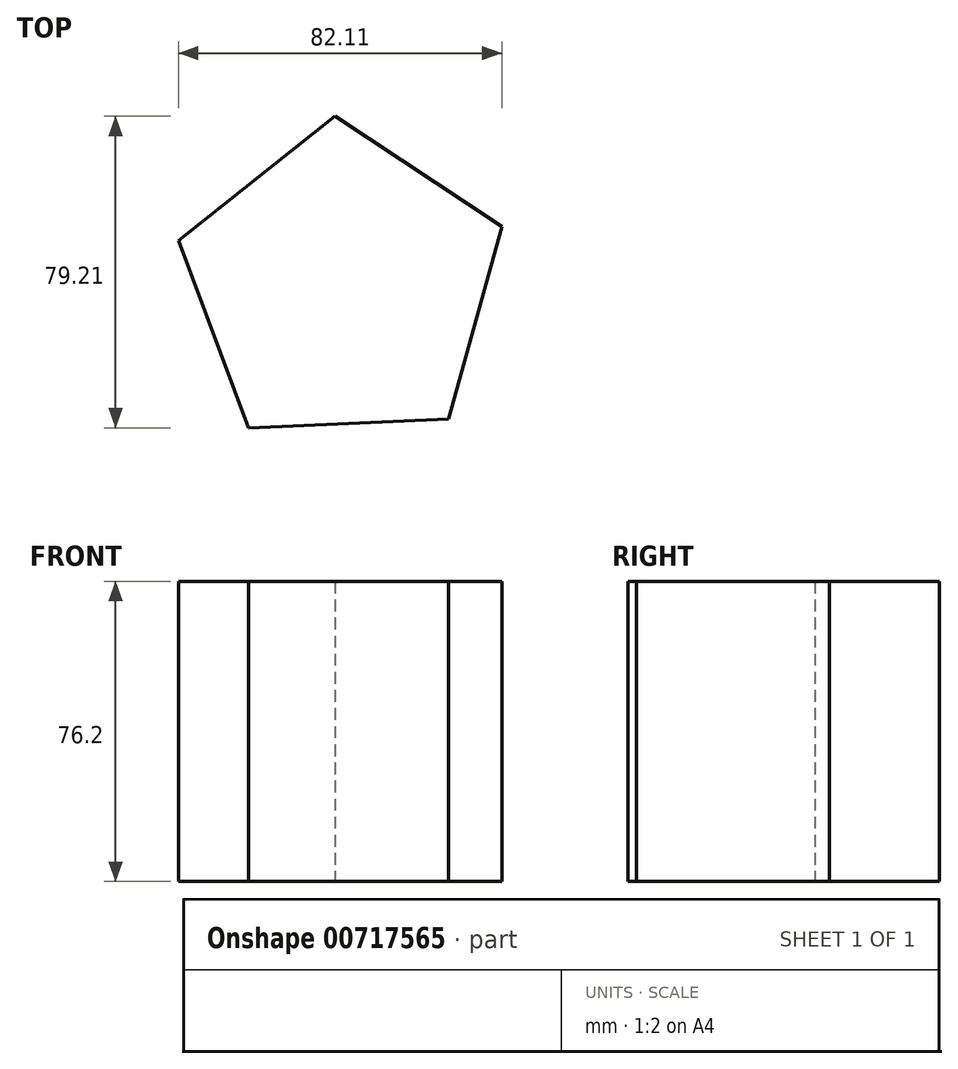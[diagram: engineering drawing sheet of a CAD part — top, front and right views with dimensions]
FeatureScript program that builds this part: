
annotation { "Feature Type Name" : "Feature", "Feature Type Description" : "" }
export const myFeature = defineFeature(function(context is Context, id is Id, definition is map)
    precondition{}
    {
        {
            var Q0;
            Q0=qCreatedBy(makeId("Top.planeOp"),FACE);
            var sketch = newSketch(context, id + "F0", { "sketchPlane" : qUnion([Q0])});
            skCircle(sketch, "E0.cCircle", {"center": v(0, 0) * mm, "radius": 34.96 * mm, "construction": true});
            skLineSegment(sketch, "E0.0", {"start": v(-1.9, 43.17) * mm, "end": v(40.47, 15.14) * mm});
            skLineSegment(sketch, "E0.1", {"start": v(40.47, 15.14) * mm, "end": v(26.9, -33.82) * mm});
            skLineSegment(sketch, "E0.2", {"start": v(26.9, -33.82) * mm, "end": v(-23.85, -36.04) * mm});
            skLineSegment(sketch, "E0.3", {"start": v(-23.85, -36.04) * mm, "end": v(-41.64, 11.54) * mm});
            skLineSegment(sketch, "E0.4", {"start": v(-41.64, 11.54) * mm, "end": v(-1.9, 43.17) * mm});
            skPoint(sketch, "E0.0.midPoint", {"position": v(19.3, 29.16) * mm});
            skSolve(sketch);
        }
        {
            var Q0;
            Q0 = qSketchRegion(id + "F0", true);
            extrude(context, id + "F1", {"entities" : qUnion([Q0]), "depth" : 76.2 * mm, "offsetDistance" : 25.4 * mm});
        }
    });
